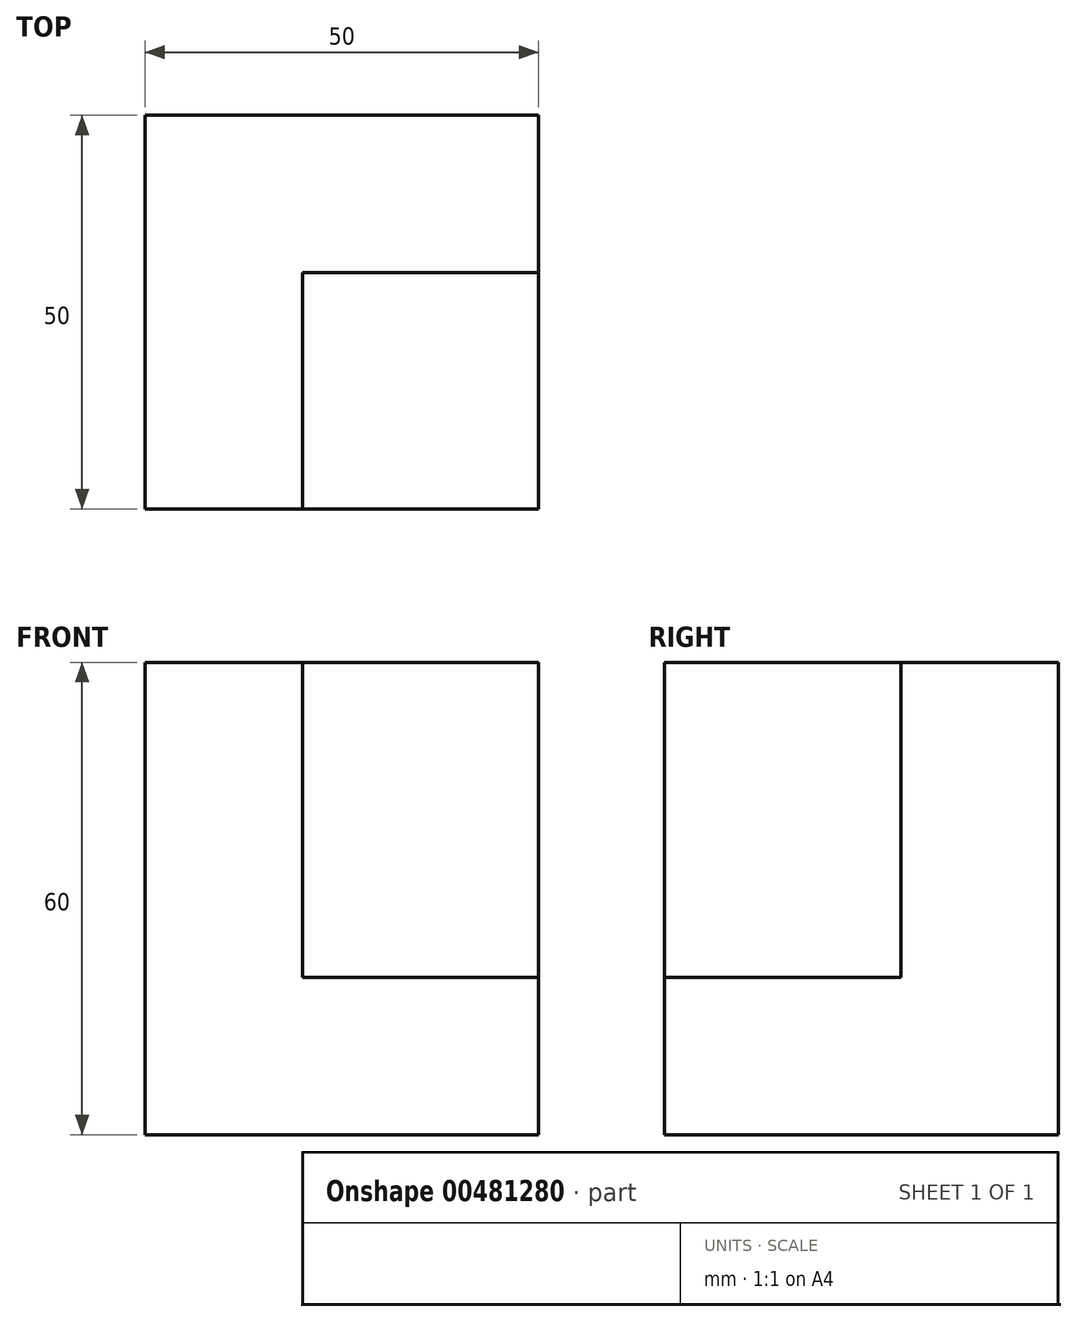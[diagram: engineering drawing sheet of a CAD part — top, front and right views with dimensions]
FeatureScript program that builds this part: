
annotation { "Feature Type Name" : "Feature", "Feature Type Description" : "" }
export const myFeature = defineFeature(function(context is Context, id is Id, definition is map)
    precondition{}
    {
        {
            var Q0;
            Q0=qCreatedBy(makeId("Front.planeOp"),FACE);
            var sketch = newSketch(context, id + "F0", { "sketchPlane" : qUnion([Q0])});
            skLineSegment(sketch, "E0", {"start": v(0, 0) * mm, "end": v(50, 0) * mm});
            skLineSegment(sketch, "E1", {"start": v(50, 0) * mm, "end": v(50, 20) * mm});
            skLineSegment(sketch, "E2", {"start": v(50, 20) * mm, "end": v(20, 20) * mm});
            skLineSegment(sketch, "E3", {"start": v(20, 20) * mm, "end": v(20, 60) * mm});
            skLineSegment(sketch, "E4", {"start": v(20, 60) * mm, "end": v(0, 60) * mm});
            skLineSegment(sketch, "E5", {"start": v(0, 60) * mm, "end": v(0, 0) * mm});
            skSolve(sketch);
        }
        {
            var Q0;
            Q0=qSketchRegion(id+"F0",true);
            extrude(context, id + "F1", {"entities" : qUnion([Q0]), "depth" : 50 * mm});
        }
        {
            var Q0;
            Q0=makeQuery(id+"F1.opExtrude","CAP_FACE",FACE,{"disambiguationData":[OSD([sQuery(id+"F0.wireOp",EDGE,"E0"),sQuery(id+"F0.wireOp",EDGE,"E1"),sQuery(id+"F0.wireOp",EDGE,"E2"),sQuery(id+"F0.wireOp",EDGE,"E3"),sQuery(id+"F0.wireOp",EDGE,"E4"),sQuery(id+"F0.wireOp",EDGE,"E5")])],"isStart":true});
            var sketch = newSketch(context, id + "F2", { "sketchPlane" : qUnion([Q0])});
            skLineSegment(sketch, "E6", {"start": v(-50, 20) * mm, "end": v(-50, 60) * mm});
            skLineSegment(sketch, "E7", {"start": v(-50, 60) * mm, "end": v(-20, 60) * mm});
            skLineSegment(sketch, "E8", {"start": v(-20, 60) * mm, "end": v(-20, 20) * mm});
            skLineSegment(sketch, "E9", {"start": v(-20, 20) * mm, "end": v(-50, 20) * mm});
            skSolve(sketch);
        }
        {
            var Q0;
            Q0 = qSketchRegion(id + "F2", true);
            extrude(context, id + "F3", {"entities" : qUnion([Q0]), "operationType" : NewBodyOperationType.ADD, "oppositeDirection" : true, "depth" : 20 * mm});
        }
    });
